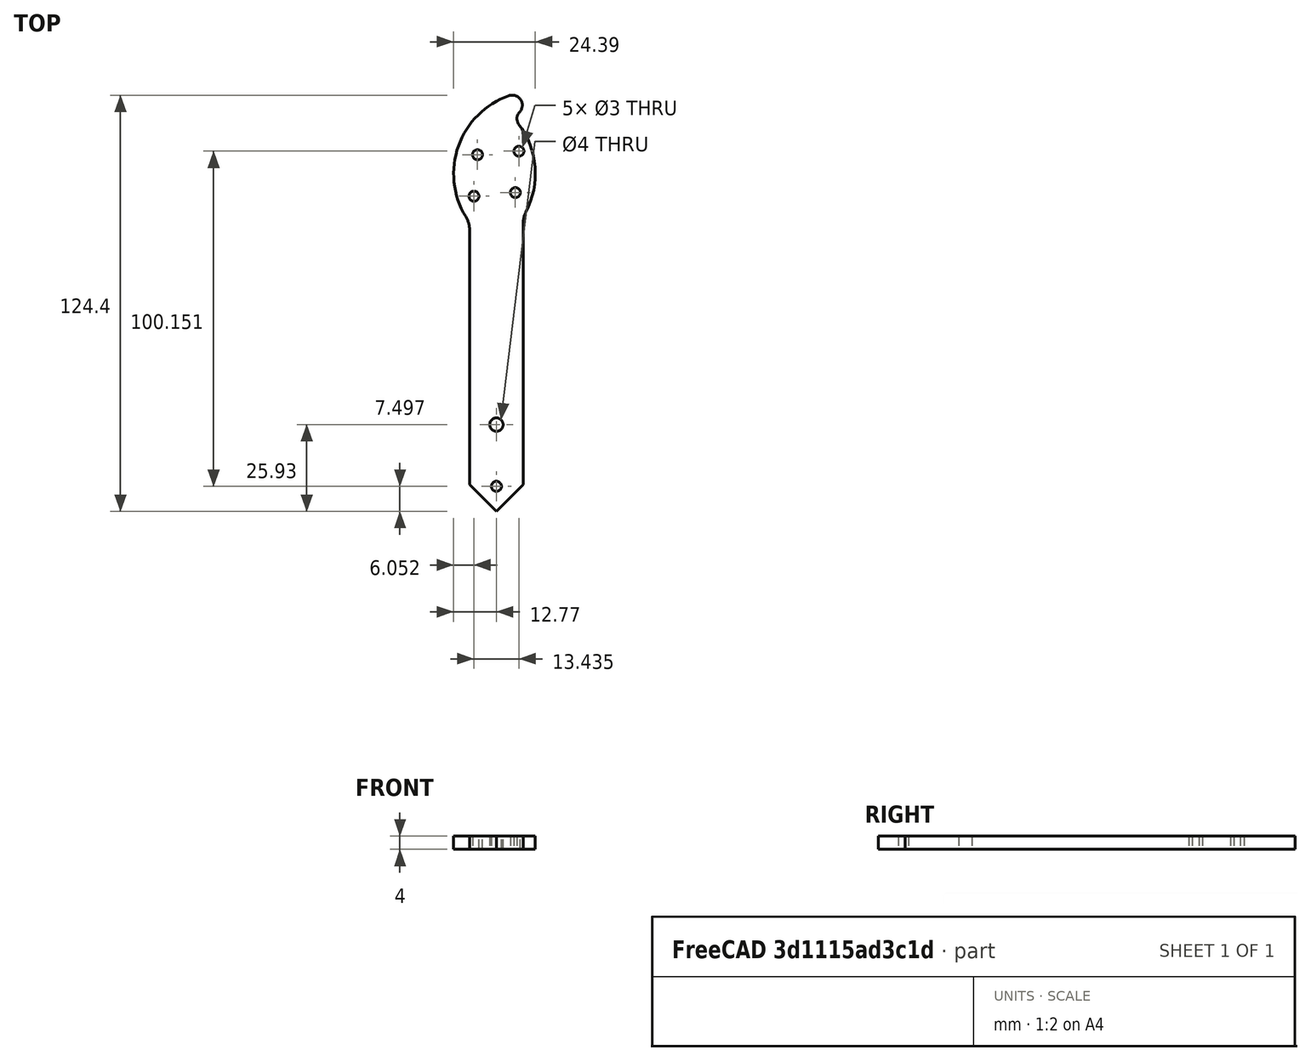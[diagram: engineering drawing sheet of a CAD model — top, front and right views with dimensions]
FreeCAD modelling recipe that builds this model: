
FCSTD DOCUMENT  (FreeCAD 0.18RUnknown)
Label: arm
License: All rights reserved
LicenseURL: http://en.wikipedia.org/wiki/All_rights_reserved
objects: Sketcher::SketchObject×1, Part::Extrusion×1, App::Part×1
note: 2 computed .brp shape members not serialized (recipe doc carries the construction recipe); baked Part::Feature solids carry a one-line shape summary decoded from their .brp

FEATURE [Sketcher::SketchObject] Sketch002
  expr: Constraints[9] = anomaly#Spreadsheet.armLength
  expr: Constraints[20] = anomaly#Spreadsheet.armOffsetElectro
  expr: Constraints[10] = anomaly#Spreadsheet.armHoleCenterOffset
  sketch-geometry (24):
    g0: LineSegment StartX=-8 StartY=-92.9332 StartZ=0 EndX=-8 EndY=-17.0009 EndZ=0
    g1: ArcOfCircle CenterX=-16 CenterY=-17.0009 CenterZ=0 NormalX=0 NormalY=0 NormalZ=1 AngleXU=0 Radius=8 StartAngle=-1.03e-13 EndAngle=0.546741
    g2: ArcOfCircle CenterX=15 CenterY=-14.7043 CenterZ=0 NormalX=0 NormalY=0 NormalZ=1 AngleXU=0 Radius=7 StartAngle=2.65925 EndAngle=3.14159
    g3: Circle [constr] CenterX=0 CenterY=0 CenterZ=0 NormalX=0 NormalY=0 NormalZ=1 AngleXU=0 Radius=8
    g4: Circle [constr] CenterX=0 CenterY=0 CenterZ=0 NormalX=0 NormalY=0 NormalZ=1 AngleXU=0 Radius=9.5
    g5: LineSegment [constr] StartX=-6.71751 StartY=-6.71751 StartZ=0 EndX=6.71751 EndY=6.71751 EndZ=0
    g6: LineSegment [constr] StartX=5.65685 StartY=-5.65685 StartZ=0 EndX=-5.65685 EndY=5.65685 EndZ=0
    g7: Circle CenterX=0 CenterY=-75 CenterZ=0 NormalX=0 NormalY=0 NormalZ=1 AngleXU=0 Radius=2
    g8: ArcOfCircle CenterX=11.9331 CenterY=0 CenterZ=0 NormalX=0 NormalY=0 NormalZ=1 AngleXU=0 Radius=24.7 StartAngle=1.90923 EndAngle=3.68833
    g9: ArcOfCircle CenterX=4.72855 CenterY=20.4691 CenterZ=0 NormalX=0 NormalY=0 NormalZ=1 AngleXU=0 Radius=3 StartAngle=5.51344 EndAngle=8.19241
    g10: ArcOfCircle CenterX=8.84318 CenterY=16.4813 CenterZ=0 NormalX=0 NormalY=0 NormalZ=1 AngleXU=0 Radius=2.73 StartAngle=2.37184 EndAngle=3.78616
    g11: ArcOfCircle CenterX=-13.0833 CenterY=0 CenterZ=0 NormalX=0 NormalY=0 NormalZ=1 AngleXU=0 Radius=24.7 StartAngle=5.80084 EndAngle=6.92775
    g12: LineSegment StartX=8 StartY=-45.0254 StartZ=0 EndX=8 EndY=-92.9332 EndZ=0
    g13: Circle CenterX=0 CenterY=-93.4332 CenterZ=0 NormalX=0 NormalY=0 NormalZ=1 AngleXU=0 Radius=1.5
    g14: LineSegment [constr] StartX=-2 StartY=-115 StartZ=0 EndX=2.32235 EndY=-115 EndZ=0
    g15: LineSegment StartX=-8 StartY=-92.9332 StartZ=0 EndX=0 EndY=-100.933 EndZ=0
    g16: LineSegment StartX=0 StartY=-100.933 StartZ=0 EndX=8 EndY=-92.9332 EndZ=0
    g17: LineSegment [constr] StartX=-8 StartY=-75 StartZ=0 EndX=8 EndY=-75 EndZ=0
    g18: LineSegment [constr] StartX=8 StartY=-45.0254 StartZ=0 EndX=-8 EndY=-45.0254 EndZ=0
    g19: Circle CenterX=6.71751 CenterY=6.71751 CenterZ=0 NormalX=0 NormalY=0 NormalZ=1 AngleXU=0 Radius=1.5
    g20: Circle CenterX=5.65685 CenterY=-5.65685 CenterZ=0 NormalX=0 NormalY=0 NormalZ=1 AngleXU=0 Radius=1.5
    g21: Circle CenterX=-6.71751 CenterY=-6.71751 CenterZ=0 NormalX=0 NormalY=0 NormalZ=1 AngleXU=0 Radius=1.5
    g22: Circle CenterX=-5.65685 CenterY=5.65685 CenterZ=0 NormalX=0 NormalY=0 NormalZ=1 AngleXU=0 Radius=1.5
    g23: LineSegment StartX=8 StartY=-14.7043 StartZ=0 EndX=8 EndY=-45.0254 EndZ=0
  constraints (67):
    c: PointOnObject(g3,g-1)
    c: Radius(g3) = 8
    c: PointOnObject(g4,g-1)
    c: Radius(g4) = 9.5
    c: PointOnObject(g4,g-2)
    c: PointOnObject(g3,g-2)
    c: Angle(g5,g6) = 1.5708
    c: PointOnObject(g7,g-2)
    c: DistanceX(g0,g12) = 16
    c: DistanceY(g14,g-1) = 115
    c: DistanceY(g14,g7) = 40
    c: Tangent(g9,g8) = -1.5708
    c: Tangent(g8,g1) = 1.5708
    c: Tangent(g10,g9) = 1.5708
    c: Tangent(g11,g10) = 1.5708
    c: Vertical(g12)
    c: Tangent(g2,g11) = 1.5708
    c: PointOnObject(g8,g-1)
    c: PointOnObject(g11,g-1)
    c: PointOnObject(g13,g-2)
    c: DistanceY(g14,g13) = 21.5668
    c: Radius(g13) = 1.5
    c: DistanceX(g9) = 4.72855
    c: DistanceY(g9) = 20.4691
    c: Horizontal(g14)
    c: Coincident(g15,g0)
    c: PointOnObject(g15,g-2)
    c: Coincident(g16,g15)
    c: Coincident(g16,g12)
    c: Radius(g8) = 24.7
    c: Radius(g9) = 3
    c: PointOnObject(g17,g0)
    c: PointOnObject(g17,g12)
    c: Horizontal(g17)
    c: Symmetric(g17,g17,g7)
    c: PointOnObject(g-1,g5)
    c: PointOnObject(g-1,g6)
    c: PointOnObject(g6,g3)
    c: PointOnObject(g6,g3)
    c: PointOnObject(g5,g4)
    c: PointOnObject(g5,g4)
    c: Angle(g6,g-1) = 0.785398
    c: Radius(g2) = 7
    c: Coincident(g18,g12)
    c: PointOnObject(g18,g0)
    c: Symmetric(g18,g12,g-2)
    c: Tangent(g0,g1) = -1.5708
    c: Radius(g1) = 8
    c: Perpendicular(g16,g15)
    c: Equal(g15,g16)
    c: DistanceY(g15,g13) = 7.5
    c: DistanceY(g2) = -11.4573
    c: Radius(g10) = 2.73
    c: Radius(g11) = 24.7
    c: Radius(g7) = 2
    c: Coincident(g19,g5)
    c: Coincident(g20,g6)
    c: Coincident(g21,g5)
    c: Coincident(g22,g6)
    c: Equal(g22,g19)
    c: Equal(g19,g20)
    c: Equal(g20,g21)
    c: Radius(g19) = 1.5
    c: Coincident(g23,g12)
    c: Vertical(g23)
    c: Tangent(g23,g2) = -1.5708
    c: DistanceY(g12) = -45.0254
FEATURE [Part::Extrusion] Extrude001
  Base = -> Sketch002
  Dir = (0,0,1)
  DirMode = 2
  FaceMakerClass = Part::FaceMakerBullseye
  LengthFwd = 0
  LengthRev = 4
  Solid = true
  Symmetric = false
FEATURE [App::Part] Part  label="Arm"
  Group = -> [Extrude001,Sketch002]
  License = CC BY 3.0
  LicenseURL = http://creativecommons.org/licenses/by/3.0/
  Origin = -> Origin
